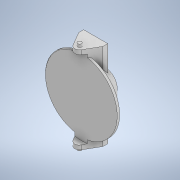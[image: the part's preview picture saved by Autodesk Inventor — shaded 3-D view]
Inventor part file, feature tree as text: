
AUTODESK INVENTOR PART (.ipt)
format: ipt  version: 2020 (Build 240168000, 168)  size: 176,128 bytes
history: native  units: in
note: dims shown in document units (in); Inventor stores cm internally (conversion verified against a paired STEP export)
features: sketch x4, extrude x3, revolve x1, mirror x1, chamfer x1
ambient origin geometry x8: Origin, YZ Plane, XZ Plane, XY Plane, X Axis, Y Axis, Z Axis, Center Point
bodies: Solid1 (feature_tree)
feature tree (10):
  extrude  "Extrusion1"  Depth=1.9685in
  revolve  "Revolution1"  [1 undecoded]
  extrude  "Extrusion2"  Depth=0.7874in
  extrude  "Extrusion3"  Depth=5.9055in
  mirror  "Mirror1"
  chamfer  "Chamfer1"  Distance=0.4724in
  sketch  "Sketch1"  dims[d0=0.7874in d1=1.9685in]
  sketch  "Sketch2"  dims[d2=60.0deg d3=1.5748in]
  sketch  "Sketch3"  dims[d4=0.7874in d5=0.7874in]
  sketch  "Sketch4"  dims[d6=14.1732in d7=0.0in d8=5.9055in d9=0.4724in d10=135.0deg d11=1.9685in d12=3.937in d13=0.3937in d14=90.0deg d15=12.8346in d16=14.1732in d17=0.0in d18=0.6299in d19=0.4724in d20=0.0in d21=0.0787in d22=0.0787in d23=45.0deg]
note: 1 required parameter value undecoded (feature->parameter linkage not recoverable at this tier; creation-order binding heuristic only, values carry confidence <= 0.55)
